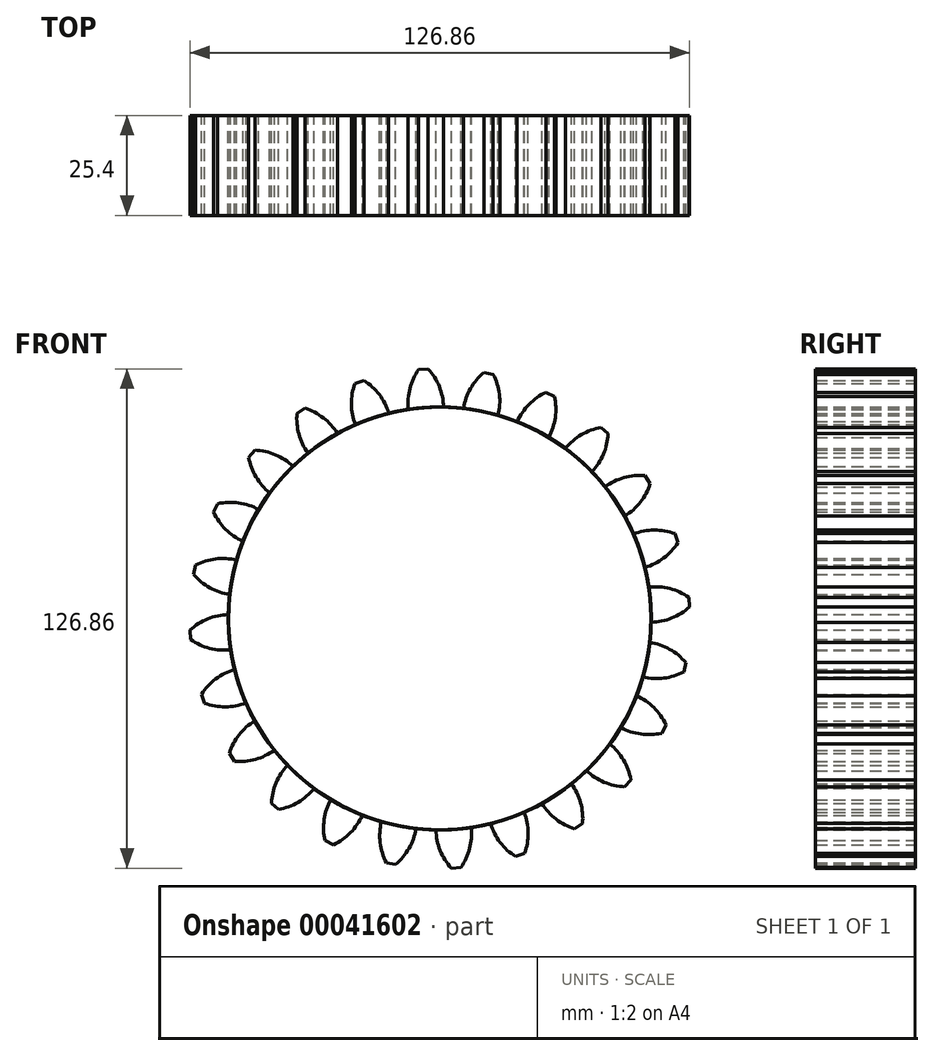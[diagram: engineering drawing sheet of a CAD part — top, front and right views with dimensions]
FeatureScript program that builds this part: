
annotation { "Feature Type Name" : "Feature", "Feature Type Description" : "" }
export const myFeature = defineFeature(function(context is Context, id is Id, definition is map)
    precondition{}
    {
        {
            var Q0;
            Q0=qCreatedBy(makeId("Front.planeOp"),FACE);
            var sketch = newSketch(context, id + "F0", { "sketchPlane" : qUnion([Q0])});
            skCircle(sketch, "E0", {"center": v(0, 0) * mm, "radius": 53.72 * mm});
            skCircle(sketch, "E1", {"center": v(0, 0) * mm, "radius": 58.67 * mm, "construction": true});
            skCircle(sketch, "E2", {"center": v(0, 0) * mm, "radius": 63.5 * mm, "construction": true});
            skLineSegment(sketch, "E3", {"start": v(0, 0) * mm, "end": v(0, 76.8) * mm, "construction": true});
            skLineSegment(sketch, "E4", {"start": v(0, 0) * mm, "end": v(-5.04, 76.92) * mm, "construction": true});
            skLineSegment(sketch, "E5", {"start": v(0, 58.67) * mm, "end": v(-86.24, 58.67) * mm, "construction": true});
            skLineSegment(sketch, "E6", {"start": v(0, 58.67) * mm, "end": v(-90.6, 25.7) * mm, "construction": true});
            skCircle(sketch, "E7", {"center": v(0, 58.67) * mm, "radius": 14.6 * mm, "construction": true});
            skCircle(sketch, "E8", {"center": v(0, 0) * mm, "radius": 55.14 * mm, "construction": true});
            skCircle(sketch, "E9", {"center": v(-13.63, 53.42) * mm, "radius": 14.6 * mm, "construction": true});
            skArc(sketch, "E10", {"start": v(0, 58.63) * mm, "mid": v(0, 58.65) * mm, "end": v(-0.02, 58.67) * mm});
            skPoint(sketch, "E11.orphan", {"position": v(-5.32, 63.28) * mm});
            skPoint(sketch, "E12.MirrorCS.start.orphan", {"position": v(-7.98, 53.13) * mm});
            skPoint(sketch, "E13.orphan", {"position": v(0.97, 53.71) * mm});
            skPoint(sketch, "E14.orphan", {"position": v(-2.99, 63.43) * mm});
            skArc(sketch, "E15", {"start": v(0.97, 53.67) * mm, "mid": v(-0.1, 58.91) * mm, "end": v(-2.96, 63.43) * mm});
            skArc(sketch, "E16.MirrorCS", {"start": v(-7.97, 53.09) * mm, "mid": v(-7.59, 58.42) * mm, "end": v(-5.35, 63.27) * mm});
            skLineSegment(sketch, "E17", {"start": v(-5.35, 63.27) * mm, "end": v(-2.96, 63.43) * mm});
            skSolve(sketch);
        }
        {
            var Q0;
            {var subQ0=sQuery(id+"F0.wireOp",EDGE,"E17");Q0=makeQuery(id+"F0.imprint","IMPRINT",FACE,{"disambiguationData":[TD([[makeQuery(id+"F0.imprint","IMPRINT",EDGE,{"derivedFrom":subQ0}),-1.0]])]});}
            var Q1;
            {var subQ0=sQuery(id+"F0.wireOp",EDGE,"E0");var subQ2=makeQuery(id+"F0.imprint","INTERSECT",VERTEX,{"derivedFrom":[subQ0,sQuery(id+"F0.wireOp",EDGE,"E15")]});Q1=makeQuery(id+"F0.imprint","IMPRINT",FACE,{"disambiguationData":[TD([[makeQuery(id+"F0.imprint","IMPRINT",EDGE,{"disambiguationData":[TD([[subQ2,-1.0]])],"derivedFrom":subQ0}),1.0]])]});}
            extrude(context, id + "F1", {"entities" : qUnion([Q0, Q1]), "depth" : 25.4 * mm});
        }
        {
            var Q0;
            Q0=makeQuery(id+"F1.opExtrude","SWEPT_BODY",BODY,{"disambiguationData":[OSD([sQuery(id+"F0.wireOp",EDGE,"E0"),sQuery(id+"F0.wireOp",EDGE,"E15"),sQuery(id+"F0.wireOp",EDGE,"E16.MirrorCS"),sQuery(id+"F0.wireOp",EDGE,"E17")])]});
            var Q1;
            Q1=makeQuery(id+"F1.opExtrude","SWEPT_FACE",FACE,{"disambiguationData":[OSD([sQuery(id+"F0.wireOp",EDGE,"E0")])]});
            circularPattern(context, id + "F2", {"entities" : qUnion([Q0]), "axis" : qUnion([Q1]), "angle" : 15 * degree, "instanceCount" : 24});
        }
    });
